# Revit family: PS2020
name_source: partatom
category: Luminarias
units: mm (PartAtom-declared; Revit-internal decimal feet)

## family parameters
Compartido = Sí
Corte con vacíos al cargar = No
Cota de conector redondo = Diámetro de uso
Origen de luz = No
Punto de cálculo de habitación = No
Se basa en plano de trabajo = Sí
Siempre vertical = No
Tipo de pieza = Normal

## types (1)
- PERFIL_PS2020
    Clips de Sujecion 2020.2 = 4
    Conector 2020.3 = 4
    Descripción = PERFIL DE ALUMINIO CIRCULAR CON DIFUSOR LECHOSO, PARA ALOJAR TIRA LUMINOSA, PERFIL DE COLOCACION DE 12.7MM DE ANCHO. INSTALACION SOBRE SUPERFICIES PLANAS (CON CLIP MONTADO), PERFIL DE SOBREPONER. IDEAL PARA ATENUAR EL BRILLO E INCORPORAR LA LUZ AL AMBIENTE.PRESENTACION DESDE 0.5 - 3 METROS, REQUEIRE ACCESORIOS COMO TAPA FINAL (CONSIDERAR 1 PAR POR SEGMENTO DE PERFIL), CLIPS DE SUJECION (CONSIDERAR 4 PZAS POR SEGMENTO DE PERFIL) Y CONECTOR PARA SUSPENDER (CONSIDERAR 4 PZAS POR SEGMENTO DE PERFIL).
    Elevación por defecto = 1219 mm
    Fabricante = BRILLANT
    Longitud = 1000 mm  [stored 3.28084 ft]
    Modelo = PS2020
    Tapa Final 2020.1 = 1

note: [stored X ft] marks values corroborated as IEEE doubles in the binary element streams (Revit-internal decimal feet)

## geometry (parser evidence)
native form markers: Blend x2
no freeform markers — native parametric forms only
